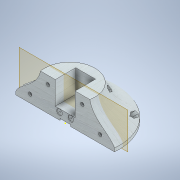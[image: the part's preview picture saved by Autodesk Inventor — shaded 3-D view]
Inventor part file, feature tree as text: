
AUTODESK INVENTOR PART (.ipt)
format: ipt  version: 2021 (Build 250183000, 183)  size: 326,656 bytes
history: native  units: mm
features: sketch x9, extrude x7, plane x2, revolve x1, split x1
ambient origin geometry x8: Origin, YZ Plane, XZ Plane, XY Plane, X Axis, Y Axis, Z Axis, Center Point
bodies: Solid1 (feature_tree)
feature tree (20):
  revolve  "Revolution1"  [1 undecoded]
  extrude  "Extrusion1"  Depth=5.0mm
  extrude  "Extrusion2"  Depth=30.0mm
  extrude  "Extrusion3"  Depth=24.0mm
  plane  "Work Plane1"
  split  "Split1"
  extrude  "Extrusion4"  Depth=35.0mm TaperAngle=0.0deg
  plane  "Work Plane2"
  extrude  "Extrusion5"  Depth=8.0mm TaperAngle=0.0deg
  sketch  "Sketch8"  dims[d14=5.2mm d15=5.2mm]
  extrude  "Extrusion6"  Depth=5.2mm
  extrude  "Extrusion7"  Depth=12.0mm
  sketch  "Sketch1"  dims[d0=75.0mm d1=50.0mm]
  sketch  "Sketch2"  dims[d2=38.0mm d3=5.0mm]
  sketch  "Sketch3"  dims[d4=90.0deg d5=30.0mm]
  sketch  "Sketch4"  dims[d6=48.0mm d7=24.0mm]
  sketch  "Sketch6"  dims[d8=15.0mm d9=35.0mm d10=0.0mm]
  sketch  "Sketch7"  dims[d11=17.0mm d12=8.0mm d13=0.0mm]
  sketch  "Sketch9"  dims[d16=12.0mm d17=12.0mm]
  sketch  "Sketch10"  dims[d18=22.0mm d19=12.0mm d20=52.0mm d21=52.0mm d22=0.0mm d23=0.0mm d24=0.0mm d25=21.0mm d26=2.5mm d27=0.0mm d28=-12.5mm d29=8.0mm d30=8.0mm d31=8.0mm d32=8.0mm d33=50.0mm d34=0.0mm d35=8.5mm d36=8.5mm d37=1.0mm d38=0.0mm d39=1.5mm d40=1.5mm d41=10.0mm d42=0.0mm]
note: 1 required parameter value undecoded (feature->parameter linkage not recoverable at this tier; creation-order binding heuristic only, values carry confidence <= 0.55)
